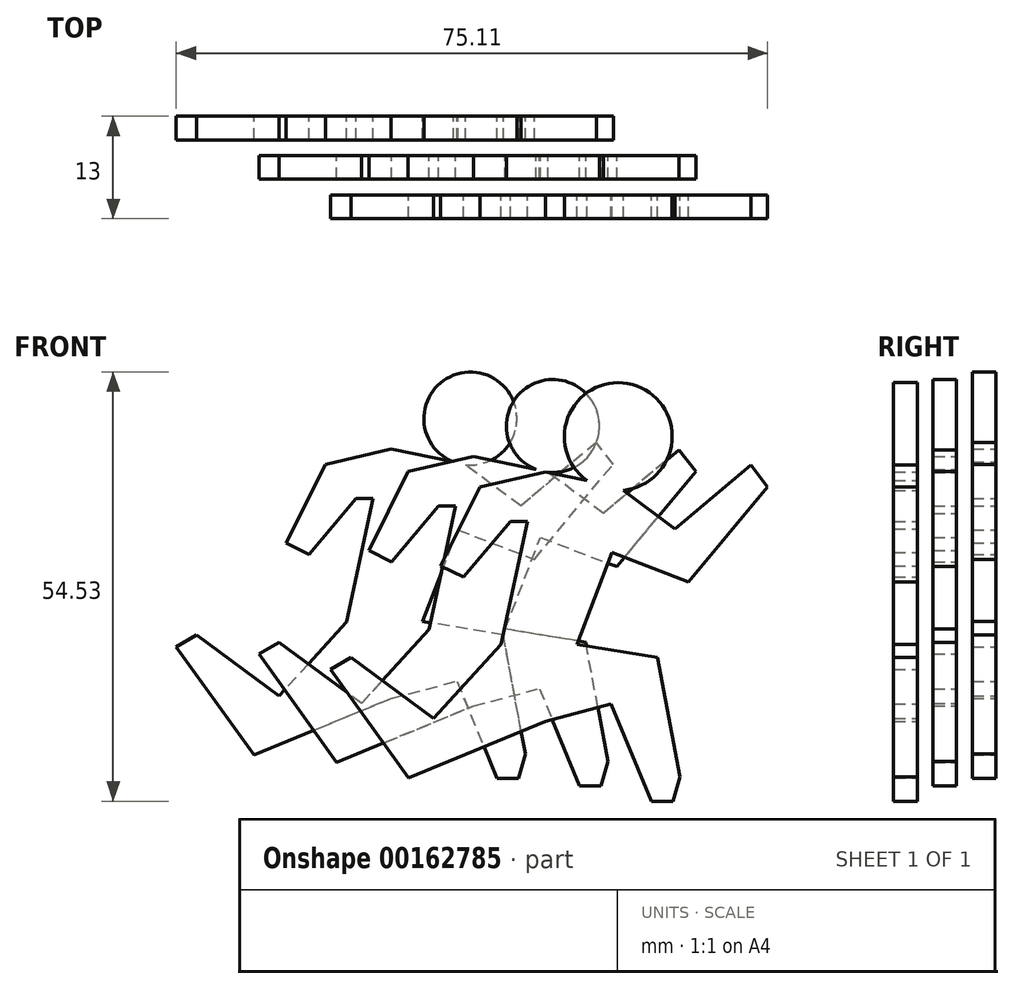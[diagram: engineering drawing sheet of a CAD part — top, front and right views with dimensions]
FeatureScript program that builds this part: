
annotation { "Feature Type Name" : "Feature", "Feature Type Description" : "" }
export const myFeature = defineFeature(function(context is Context, id is Id, definition is map)
    precondition{}
    {
        {
            var Q0;
            Q0=qCreatedBy(makeId("Front.planeOp"),FACE);
            var sketch = newSketch(context, id + "F0", { "sketchPlane" : qUnion([Q0])});
            skCircle(sketch, "E0", {"center": v(4, 46.32) * mm, "radius": 6.85 * mm});
            skLineSegment(sketch, "E1", {"start": v(0, 40.76) * mm, "end": v(-5.24, 41.84) * mm});
            skLineSegment(sketch, "E2", {"start": v(-5.24, 41.84) * mm, "end": v(-13.57, 39.91) * mm});
            skLineSegment(sketch, "E3", {"start": v(-13.57, 39.91) * mm, "end": v(-18.57, 29.91) * mm});
            skLineSegment(sketch, "E4", {"start": v(-18.57, 29.91) * mm, "end": v(-15.7, 28.48) * mm});
            skLineSegment(sketch, "E5", {"start": v(-15.7, 28.48) * mm, "end": v(-9.73, 35.56) * mm});
            skLineSegment(sketch, "E6", {"start": v(-9.73, 35.56) * mm, "end": v(-7.55, 35.56) * mm});
            skLineSegment(sketch, "E7", {"start": v(-7.55, 35.56) * mm, "end": v(-10.88, 19.92) * mm});
            skLineSegment(sketch, "E8", {"start": v(-10.88, 19.92) * mm, "end": v(-19.48, 10.5) * mm});
            skLineSegment(sketch, "E9", {"start": v(-19.48, 10.5) * mm, "end": v(-29.98, 18.25) * mm});
            skLineSegment(sketch, "E10", {"start": v(-29.98, 18.25) * mm, "end": v(-32.53, 16.74) * mm});
            skLineSegment(sketch, "E11", {"start": v(-32.53, 16.74) * mm, "end": v(-22.67, 3) * mm});
            skLineSegment(sketch, "E12", {"start": v(-22.67, 3) * mm, "end": v(-5.24, 10.17) * mm});
            skLineSegment(sketch, "E13", {"start": v(-5.24, 10.17) * mm, "end": v(3.1, 12.35) * mm});
            skLineSegment(sketch, "E14", {"start": v(3.1, 12.35) * mm, "end": v(8.22, 0) * mm});
            skLineSegment(sketch, "E15", {"start": v(8.22, 0) * mm, "end": v(10.91, 0) * mm});
            skLineSegment(sketch, "E16", {"start": v(10.91, 0) * mm, "end": v(11.81, 3.12) * mm});
            skLineSegment(sketch, "E17", {"start": v(11.81, 3.12) * mm, "end": v(9, 18.25) * mm});
            skLineSegment(sketch, "E18", {"start": v(9, 18.25) * mm, "end": v(-1.26, 19.92) * mm});
            skLineSegment(sketch, "E19", {"start": v(-1.26, 19.92) * mm, "end": v(3.22, 31.58) * mm});
            skLineSegment(sketch, "E20", {"start": v(3.22, 31.58) * mm, "end": v(12.93, 27.85) * mm});
            skLineSegment(sketch, "E21", {"start": v(12.93, 27.85) * mm, "end": v(22.96, 39.91) * mm});
            skLineSegment(sketch, "E22", {"start": v(22.96, 39.91) * mm, "end": v(20.82, 42.7) * mm});
            skLineSegment(sketch, "E23", {"start": v(20.82, 42.7) * mm, "end": v(11.22, 34.63) * mm});
            skLineSegment(sketch, "E24", {"start": v(11.22, 34.63) * mm, "end": v(4.65, 39.5) * mm});
            skSolve(sketch);
        }
        {
            var Q0;
            {var subQ0=sQuery(id+"F0.wireOp",EDGE,"E0");var subQ1=makeQuery(id+"F0.imprint","INTERSECT",VERTEX,{"derivedFrom":[subQ0,sQuery(id+"F0.wireOp",EDGE,"E1")]});Q0=makeQuery(id+"F0.imprint","IMPRINT",FACE,{"disambiguationData":[TD([[makeQuery(id+"F0.imprint","IMPRINT",EDGE,{"disambiguationData":[TD([[subQ1,-1.0]])],"derivedFrom":subQ0}),1.0]])]});}
            var Q1;
            {var subQ0=sQuery(id+"F0.wireOp",EDGE,"E1");Q1=makeQuery(id+"F0.imprint","IMPRINT",FACE,{"disambiguationData":[TD([[makeQuery(id+"F0.imprint","IMPRINT",EDGE,{"derivedFrom":subQ0}),1.0]])]});}
            extrude(context, id + "F1", {"entities" : qUnion([Q0, Q1]), "depth" : 3 * mm});
        }
        {
            var Q0;
            Q0=qCreatedBy(makeId("Front.planeOp"),FACE);
            cPlane(context, id + "F2", {"entities" : qUnion([Q0]), "cplaneType" : CPlaneType.OFFSET, "offset" : 5 * mm, "oppositeDirection" : true, "width" : 150 * mm, "height" : 150 * mm});
        }
        {
            var Q0;
            Q0=qCreatedBy(id+"F2.planeOp",FACE);
            var sketch = newSketch(context, id + "F3", { "sketchPlane" : qUnion([Q0])});
            skCircle(sketch, "E25", {"center": v(-4.31, 47.67) * mm, "radius": 5.9 * mm});
            skLineSegment(sketch, "E26", {"start": v(-6.44, 42.16) * mm, "end": v(-14.37, 43.8) * mm});
            skLineSegment(sketch, "E27", {"start": v(-14.37, 43.8) * mm, "end": v(-22.7, 41.87) * mm});
            skLineSegment(sketch, "E28", {"start": v(-22.7, 41.87) * mm, "end": v(-27.7, 31.87) * mm});
            skLineSegment(sketch, "E29", {"start": v(-27.7, 31.87) * mm, "end": v(-24.83, 30.43) * mm});
            skLineSegment(sketch, "E30", {"start": v(-24.83, 30.43) * mm, "end": v(-18.85, 37.5) * mm});
            skLineSegment(sketch, "E31", {"start": v(-18.85, 37.5) * mm, "end": v(-16.67, 37.5) * mm});
            skLineSegment(sketch, "E32", {"start": v(-16.67, 37.5) * mm, "end": v(-20.02, 21.83) * mm});
            skLineSegment(sketch, "E33", {"start": v(-20.02, 21.83) * mm, "end": v(-28.61, 12.46) * mm});
            skLineSegment(sketch, "E34", {"start": v(-28.61, 12.46) * mm, "end": v(-39.1, 20.2) * mm});
            skLineSegment(sketch, "E35", {"start": v(-39.1, 20.2) * mm, "end": v(-41.66, 18.69) * mm});
            skLineSegment(sketch, "E36", {"start": v(-41.66, 18.69) * mm, "end": v(-31.8, 4.95) * mm});
            skLineSegment(sketch, "E37", {"start": v(-31.8, 4.95) * mm, "end": v(-14.37, 12.13) * mm});
            skLineSegment(sketch, "E38", {"start": v(-14.37, 12.13) * mm, "end": v(-6.03, 14.3) * mm});
            skLineSegment(sketch, "E39", {"start": v(-6.03, 14.3) * mm, "end": v(-0.9, 1.95) * mm});
            skLineSegment(sketch, "E40", {"start": v(-0.9, 1.95) * mm, "end": v(1.79, 1.95) * mm});
            skLineSegment(sketch, "E41", {"start": v(1.79, 1.95) * mm, "end": v(2.68, 5.08) * mm});
            skLineSegment(sketch, "E42", {"start": v(2.68, 5.08) * mm, "end": v(-0.14, 20.2) * mm});
            skLineSegment(sketch, "E43", {"start": v(-0.14, 20.2) * mm, "end": v(-10.4, 21.87) * mm});
            skLineSegment(sketch, "E44", {"start": v(-10.4, 21.87) * mm, "end": v(-5.9, 33.54) * mm});
            skLineSegment(sketch, "E45", {"start": v(-5.9, 33.54) * mm, "end": v(3.8, 29.8) * mm});
            skLineSegment(sketch, "E46", {"start": v(3.8, 29.8) * mm, "end": v(13.84, 41.87) * mm});
            skLineSegment(sketch, "E47", {"start": v(13.84, 41.87) * mm, "end": v(11.7, 44.66) * mm});
            skLineSegment(sketch, "E48", {"start": v(11.7, 44.66) * mm, "end": v(2.09, 36.58) * mm});
            skLineSegment(sketch, "E49", {"start": v(2.09, 36.58) * mm, "end": v(-4.93, 41.8) * mm});
            skSolve(sketch);
        }
        {
            var Q0;
            {var subQ0=sQuery(id+"F3.wireOp",EDGE,"E26");Q0=makeQuery(id+"F3.imprint","IMPRINT",FACE,{"disambiguationData":[TD([[makeQuery(id+"F3.imprint","IMPRINT",EDGE,{"derivedFrom":subQ0}),1.0]])]});}
            var Q1;
            {var subQ0=sQuery(id+"F3.wireOp",EDGE,"E25");var subQ1=makeQuery(id+"F3.imprint","INTERSECT",VERTEX,{"derivedFrom":[subQ0,sQuery(id+"F3.wireOp",EDGE,"E26")]});Q1=makeQuery(id+"F3.imprint","IMPRINT",FACE,{"disambiguationData":[TD([[makeQuery(id+"F3.imprint","IMPRINT",EDGE,{"disambiguationData":[TD([[subQ1,-1.0]])],"derivedFrom":subQ0}),1.0]])]});}
            extrude(context, id + "F4", {"entities" : qUnion([Q0, Q1]), "depth" : 3 * mm});
        }
        {
            var Q0;
            Q0=qCreatedBy(id+"F2.planeOp",FACE);
            cPlane(context, id + "F5", {"entities" : qUnion([Q0]), "cplaneType" : CPlaneType.OFFSET, "offset" : 5 * mm, "oppositeDirection" : true, "width" : 150 * mm, "height" : 150 * mm});
        }
        {
            var Q0;
            Q0=qCreatedBy(id+"F5.planeOp",FACE);
            var sketch = newSketch(context, id + "F6", { "sketchPlane" : qUnion([Q0])});
            skCircle(sketch, "E50", {"center": v(-14.8, 48.62) * mm, "radius": 5.9 * mm});
            skLineSegment(sketch, "E51", {"start": v(-16.93, 43.11) * mm, "end": v(-24.85, 44.74) * mm});
            skLineSegment(sketch, "E52", {"start": v(-24.85, 44.74) * mm, "end": v(-33.18, 42.82) * mm});
            skLineSegment(sketch, "E53", {"start": v(-33.18, 42.82) * mm, "end": v(-38.18, 32.82) * mm});
            skLineSegment(sketch, "E54", {"start": v(-38.18, 32.82) * mm, "end": v(-35.3, 31.38) * mm});
            skLineSegment(sketch, "E55", {"start": v(-35.3, 31.38) * mm, "end": v(-29.34, 38.46) * mm});
            skLineSegment(sketch, "E56", {"start": v(-29.34, 38.46) * mm, "end": v(-27.16, 38.46) * mm});
            skLineSegment(sketch, "E57", {"start": v(-27.16, 38.46) * mm, "end": v(-30.5, 22.77) * mm});
            skLineSegment(sketch, "E58", {"start": v(-30.5, 22.77) * mm, "end": v(-39.1, 13.4) * mm});
            skLineSegment(sketch, "E59", {"start": v(-39.1, 13.4) * mm, "end": v(-49.6, 21.15) * mm});
            skLineSegment(sketch, "E60", {"start": v(-49.6, 21.15) * mm, "end": v(-52.15, 19.64) * mm});
            skLineSegment(sketch, "E61", {"start": v(-52.15, 19.64) * mm, "end": v(-42.28, 5.9) * mm});
            skLineSegment(sketch, "E62", {"start": v(-42.28, 5.9) * mm, "end": v(-24.85, 13.07) * mm});
            skLineSegment(sketch, "E63", {"start": v(-24.85, 13.07) * mm, "end": v(-16.52, 15.25) * mm});
            skLineSegment(sketch, "E64", {"start": v(-16.52, 15.25) * mm, "end": v(-11.39, 2.9) * mm});
            skLineSegment(sketch, "E65", {"start": v(-11.39, 2.9) * mm, "end": v(-8.7, 2.9) * mm});
            skLineSegment(sketch, "E66", {"start": v(-8.7, 2.9) * mm, "end": v(-7.8, 6.02) * mm});
            skLineSegment(sketch, "E67", {"start": v(-7.8, 6.02) * mm, "end": v(-10.62, 21.15) * mm});
            skLineSegment(sketch, "E68", {"start": v(-10.62, 21.15) * mm, "end": v(-20.88, 22.82) * mm});
            skLineSegment(sketch, "E69", {"start": v(-20.88, 22.82) * mm, "end": v(-16.39, 34.48) * mm});
            skLineSegment(sketch, "E70", {"start": v(-16.39, 34.48) * mm, "end": v(-6.68, 30.75) * mm});
            skLineSegment(sketch, "E71", {"start": v(-6.68, 30.75) * mm, "end": v(3.35, 42.82) * mm});
            skLineSegment(sketch, "E72", {"start": v(3.35, 42.82) * mm, "end": v(1.2, 45.6) * mm});
            skLineSegment(sketch, "E73", {"start": v(1.2, 45.6) * mm, "end": v(-8.4, 37.53) * mm});
            skLineSegment(sketch, "E74", {"start": v(-8.4, 37.53) * mm, "end": v(-15.42, 42.75) * mm});
            skSolve(sketch);
        }
        {
            var Q0;
            {var subQ0=sQuery(id+"F6.wireOp",EDGE,"E50");var subQ1=makeQuery(id+"F6.imprint","INTERSECT",VERTEX,{"derivedFrom":[subQ0,sQuery(id+"F6.wireOp",EDGE,"E51")]});Q0=makeQuery(id+"F6.imprint","IMPRINT",FACE,{"disambiguationData":[TD([[makeQuery(id+"F6.imprint","IMPRINT",EDGE,{"disambiguationData":[TD([[subQ1,-1.0]])],"derivedFrom":subQ0}),1.0]])]});}
            var Q1;
            {var subQ0=sQuery(id+"F6.wireOp",EDGE,"E51");Q1=makeQuery(id+"F6.imprint","IMPRINT",FACE,{"disambiguationData":[TD([[makeQuery(id+"F6.imprint","IMPRINT",EDGE,{"derivedFrom":subQ0}),1.0]])]});}
            extrude(context, id + "F7", {"entities" : qUnion([Q0, Q1]), "depth" : 3 * mm});
        }
    });
